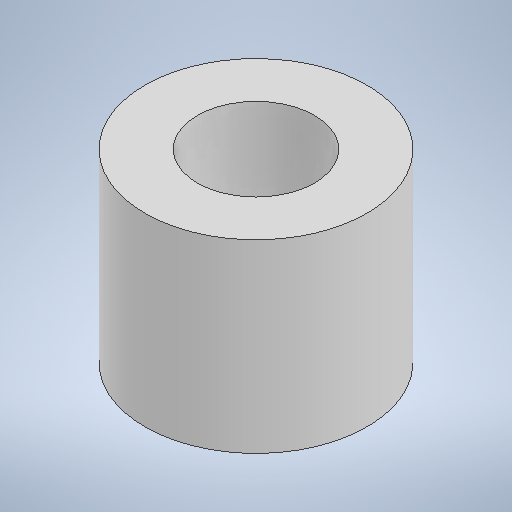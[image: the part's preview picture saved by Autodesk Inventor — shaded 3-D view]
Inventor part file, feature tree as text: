
AUTODESK INVENTOR PART (.ipt)
format: ipt  version: 2025.2 (Build 292293000, 293)  size: 203,776 bytes
history: native  units: mm
features: extrude x2, sketch x2
ambient origin geometry x8: Origin, YZ Plane, XZ Plane, XY Plane, X Axis, Y Axis, Z Axis, Center Point
bodies: Body1 (feature_tree)
feature tree (4):
  extrude  "Extrusion3"  Depth=3.0mm TaperAngle=0.0deg
  extrude  "Extrusion4"  Depth=3.0mm TaperAngle=0.0deg
  sketch  "Sketch3"  dims[d6=3.6mm d7=3.0mm d8=0.0mm]
  sketch  "Sketch4"  dims[d9=1.9mm d10=3.0mm d11=0.0mm]
